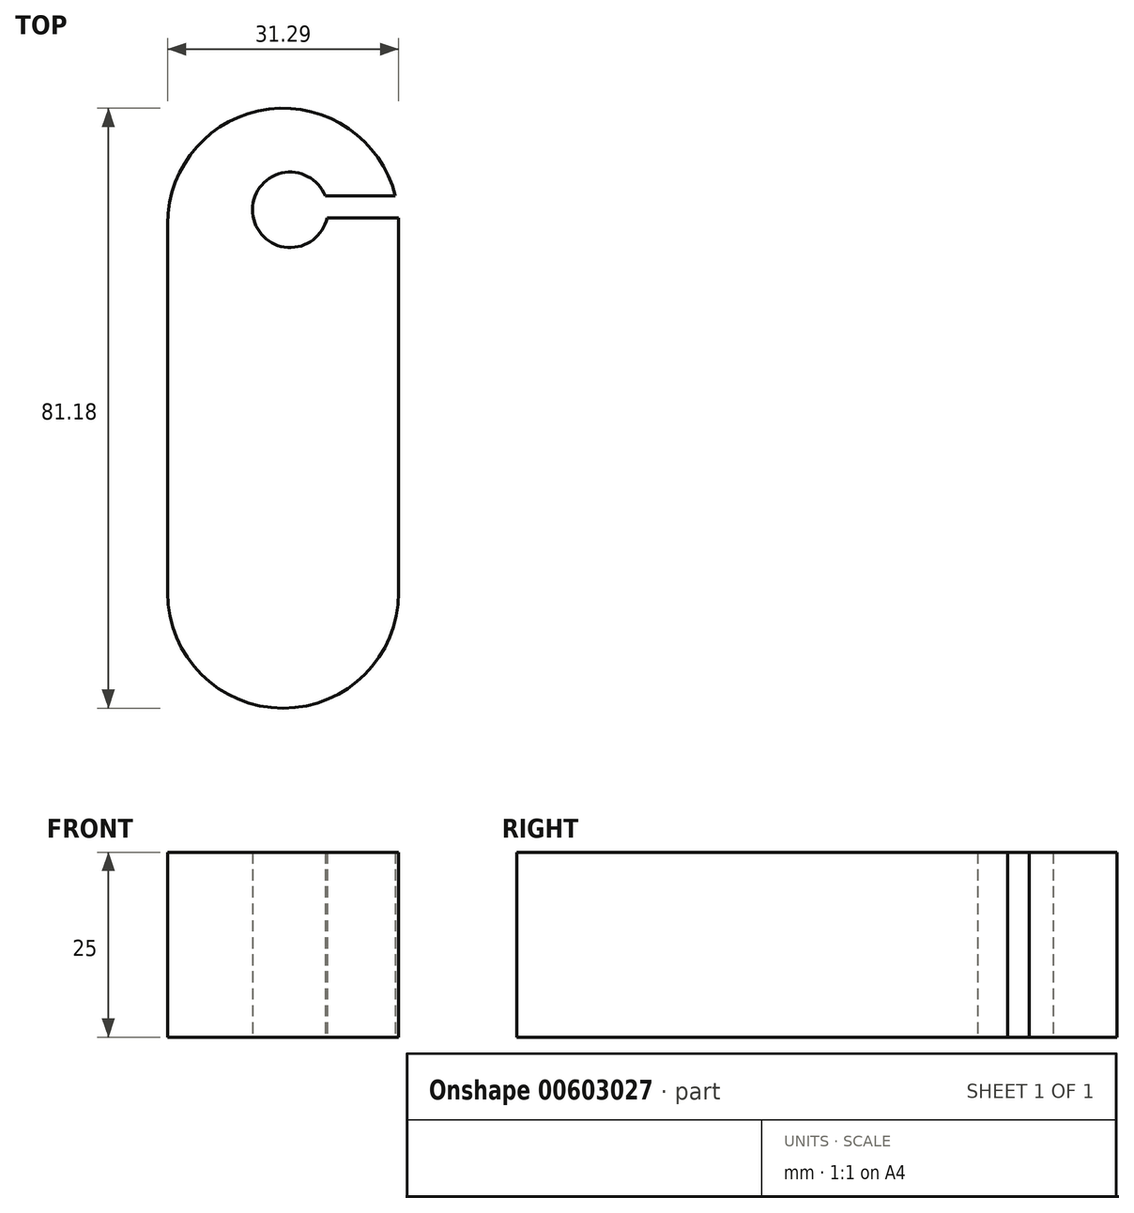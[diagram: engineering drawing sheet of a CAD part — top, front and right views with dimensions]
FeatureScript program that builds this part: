
annotation { "Feature Type Name" : "Feature", "Feature Type Description" : "" }
export const myFeature = defineFeature(function(context is Context, id is Id, definition is map)
    precondition{}
    {
        {
            var Q0;
            Q0=qCreatedBy(makeId("Top.planeOp"),FACE);
            var sketch = newSketch(context, id + "F0", { "sketchPlane" : qUnion([Q0])});
            skLineSegment(sketch, "E0.bottom", {"start": v(-16.6, 24.1) * mm, "end": v(14.7, 24.1) * mm});
            skLineSegment(sketch, "E0.top", {"start": v(-16.6, -25.8) * mm, "end": v(14.7, -25.8) * mm});
            skLineSegment(sketch, "E0.left", {"start": v(-16.6, 24.1) * mm, "end": v(-16.6, -25.8) * mm});
            skLineSegment(sketch, "E0.right", {"start": v(14.7, 24.1) * mm, "end": v(14.7, -25.8) * mm});
            skArc(sketch, "E1", {"start": v(14.7, 24.1) * mm, "mid": v(-0.95, 39.74) * mm, "end": v(-16.6, 24.1) * mm});
            skArc(sketch, "E2", {"start": v(-16.6, -25.8) * mm, "mid": v(-0.95, -41.44) * mm, "end": v(14.7, -25.8) * mm});
            skSolve(sketch);
        }
        {
            var Q0;
            Q0=makeQuery(id+"F0.imprint","IMPRINT",FACE,{"disambiguationData":[TD([[makeQuery(id+"F0.imprint","IMPRINT",EDGE,{"derivedFrom":sQuery(id+"F0.wireOp",EDGE,"E0.bottom")}),1.0]])]});
            var Q1;
            Q1=makeQuery(id+"F0.imprint","IMPRINT",FACE,{"disambiguationData":[TD([[makeQuery(id+"F0.imprint","IMPRINT",EDGE,{"derivedFrom":sQuery(id+"F0.wireOp",EDGE,"E0.bottom")}),-1.0]])]});
            var Q2;
            Q2=makeQuery(id+"F0.imprint","IMPRINT",FACE,{"disambiguationData":[TD([[makeQuery(id+"F0.imprint","IMPRINT",EDGE,{"derivedFrom":sQuery(id+"F0.wireOp",EDGE,"E0.top")}),-1.0]])]});
            extrude(context, id + "F1", {"entities" : qUnion([Q0, Q1, Q2]), "depth" : 25 * mm, "offsetDistance" : 25 * mm});
        }
        {
            var Q0;
            Q0=qCreatedBy(makeId("Top.planeOp"),FACE);
            var sketch = newSketch(context, id + "F2", { "sketchPlane" : qUnion([Q0])});
            skCircle(sketch, "E3", {"center": v(0, 26) * mm, "radius": 5.1 * mm});
            skSolve(sketch);
        }
        {
            var Q0;
            Q0 = qSketchRegion(id + "F2", true);
            extrude(context, id + "F3", {"entities" : qUnion([Q0]), "operationType" : NewBodyOperationType.REMOVE, "depth" : 25 * mm, "offsetDistance" : 25 * mm});
        }
        {
            var Q0;
            Q0=makeQuery(id+"F1.opExtrude","CAP_FACE",FACE,{"disambiguationData":[OSD([sQuery(id+"F0.wireOp",EDGE,"E0.left"),sQuery(id+"F0.wireOp",EDGE,"E0.right"),sQuery(id+"F0.wireOp",EDGE,"E1"),sQuery(id+"F0.wireOp",EDGE,"E2")])],"isStart":true});
            var sketch = newSketch(context, id + "F4", { "sketchPlane" : qUnion([Q0])});
            skLineSegment(sketch, "E4.bottom", {"start": v(2.89, -24.93) * mm, "end": v(26.36, -24.93) * mm});
            skLineSegment(sketch, "E4.top", {"start": v(2.89, -27.87) * mm, "end": v(26.36, -27.87) * mm});
            skLineSegment(sketch, "E4.left", {"start": v(2.89, -24.93) * mm, "end": v(2.89, -27.87) * mm});
            skLineSegment(sketch, "E4.right", {"start": v(26.36, -24.93) * mm, "end": v(26.36, -27.87) * mm});
            skSolve(sketch);
        }
        {
            var Q0;
            Q0 = qSketchRegion(id + "F4", true);
            extrude(context, id + "F5", {"entities" : qUnion([Q0]), "operationType" : NewBodyOperationType.REMOVE, "oppositeDirection" : true, "depth" : 25 * mm, "offsetDistance" : 25 * mm});
        }
    });
